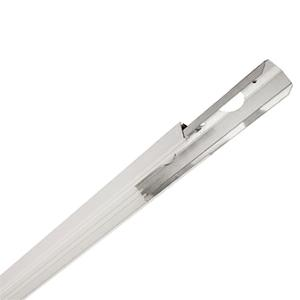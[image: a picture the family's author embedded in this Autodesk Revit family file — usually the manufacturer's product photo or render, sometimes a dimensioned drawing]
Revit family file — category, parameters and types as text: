
# Revit family: 3f_filippi_-_3f_linux_s-nl_ip40_3f_filippi_-_a20011_-_3f_linux_s_nl_l3556
name_source: partatom
category: Lighting Fixtures
units: mm (PartAtom-declared; Revit-internal decimal feet)

## family parameters
Cut with Voids When Loaded = No
Host = Face
Light Source = No
Part Type = Normal
Room Calculation Point = No
Round Connector Dimension = Use Diameter
Shared = No

## types (1)
- 3F Filippi - 3F Linux S-NL IP40
    Apparent Load = 0 VA
    Default Elevation = 1800 mm
    Description = Supporting structure WITHOUT power supply line for continuous channels, suitable for transporting power lines or mounting luminaires.

MECHANICAL
Wired base in hot galvanised steel and painted with polyester base in white colour, obtained through rolling process.
Saline-mist resistance equal to 500hrs and damp resistance equal to 700hrs.
Linear connecting element in hot galvanised steel already mounted on one end to form continuous channels.
Polycarbonate reinforced cable supports (for use every 500 mm approx.).
Dimensions: 3556x62 mm, height 38 mm. Weight 3.28 kg.
IP40 protection degree.

ELECTRICAL
Feeding input on top (at the beginning or in the middle of the structure).

INSTALLATION
Suspended.
All accessories dedicated to this product are available on the Catalog and on our website www.3F-Filippi.com.

WARNING
Luminaire designed for disposal/recycling at end-of-life.
    Height = 38 mm
    Lamp = 0 x
    Length = 3556 mm
    Luminous efficacy = 0 lm/W
    Manufacturer = 3F Filippi
    ModVariant = No
    Model = 3F Filippi - A20011 - 3F Linux S NL L3556
    Mounting Place = Ceiling
    Mounting Type = Pendant
    Number of Poles = 1
    OnlyDefault = Yes
    Power Factor = 1
    Product Name = 3F Filippi - 3F Linux S-NL IP40
    Product group = Accessories
    ProductGroupID = 98
    Protection Class = Protection class
    Protection Degree = IP 40
    RLX_Detail_Level = 1
    RLX_Emergency_Light_Flux = 0 lm
    RLX_Emergency_Type = 0
    RLX_Emergency_Type_DB = No
    RlxData = <blob elided: 39365 chars, md5=aad3abf7>
    Standby Power = 0 W
    System Light Flux = 0 lm
    System Power = 0 W
    Type Comments = Product without accessories
    Type Image = 3ffilippi_3f_linux_s-n_ip40_l3556.jpg
    URL = http://relux.com
    VarID = ---
    Voltage = 0 V
    Weight = 0.00 kg
    Width = 62 mm  [stored 0.203412 ft]

note: [stored X ft] marks values corroborated as IEEE doubles in the binary element streams (Revit-internal decimal feet)

## geometry (parser evidence)
native form markers: Blend x4, Sweep x13
no freeform markers — native parametric forms only
